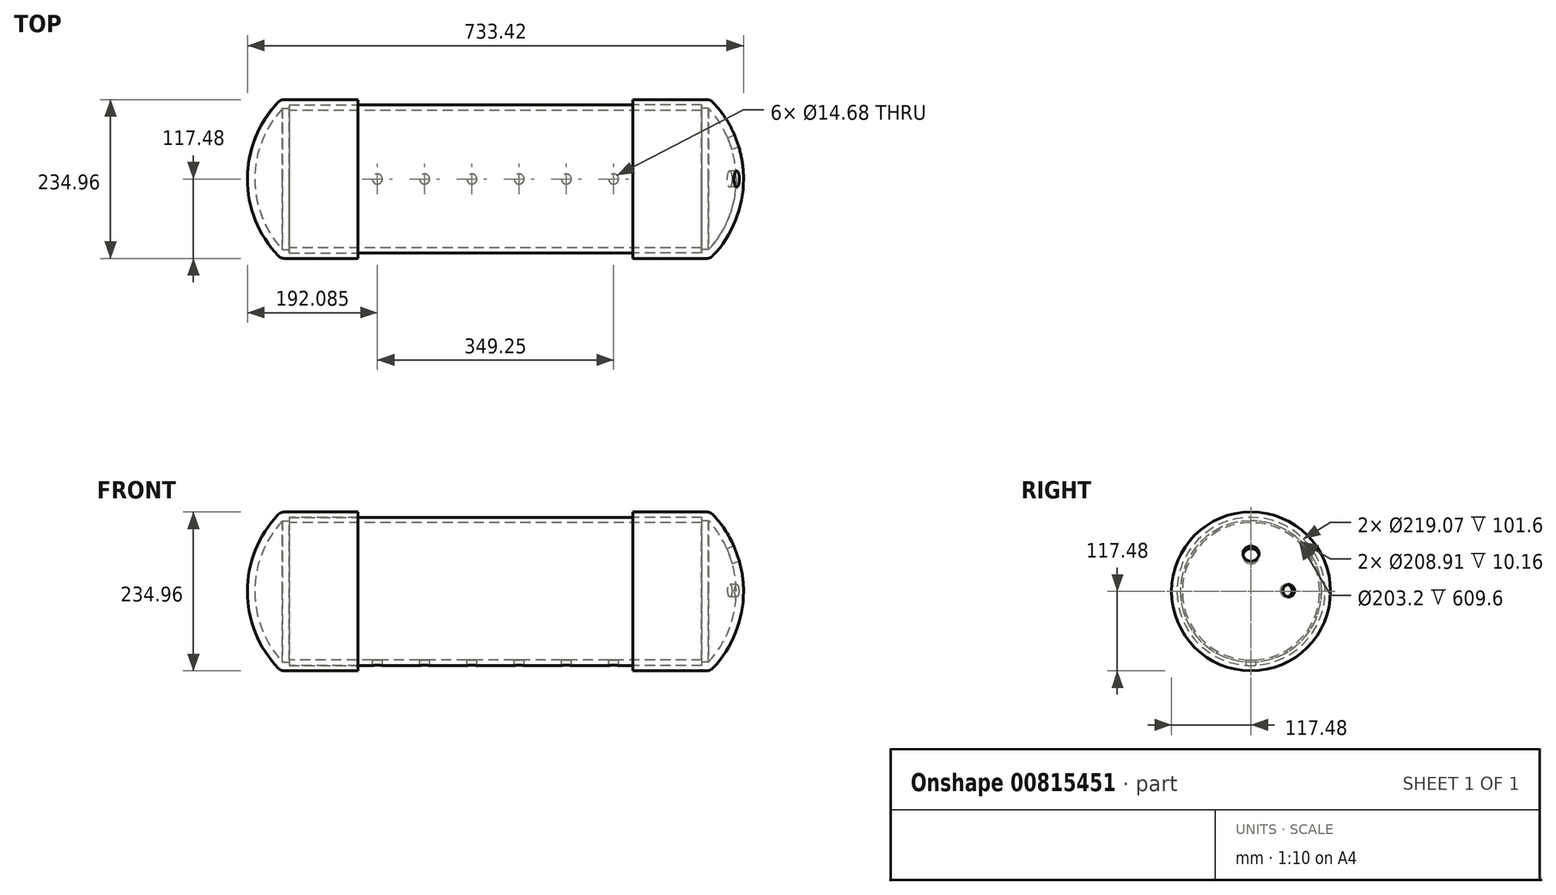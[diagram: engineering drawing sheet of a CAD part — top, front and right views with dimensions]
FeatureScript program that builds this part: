
annotation { "Feature Type Name" : "Feature", "Feature Type Description" : "" }
export const myFeature = defineFeature(function(context is Context, id is Id, definition is map)
    precondition{}
    {
        {
            var Q0;
            Q0=qCreatedBy(makeId("Right.planeOp"),FACE);
            var sketch = newSketch(context, id + "F0", { "sketchPlane" : qUnion([Q0])});
            skCircle(sketch, "E0", {"center": v(0, 0) * mm, "radius": 109.54 * mm});
            skCircle(sketch, "E1", {"center": v(0, 0) * mm, "radius": 101.6 * mm});
            skSolve(sketch);
        }
        {
            var Q0;
            Q0=makeQuery(id+"F0.imprint","IMPRINT",FACE,{"disambiguationData":[TD([[makeQuery(id+"F0.imprint","IMPRINT",EDGE,{"derivedFrom":sQuery(id+"F0.wireOp",EDGE,"E0")}),1.0]])]});
            extrude(context, id + "F1", {"entities" : qUnion([Q0]), "depth" : 304.8 * mm, "offsetDistance" : 25.4 * mm, "hasSecondDirection" : true, "secondDirectionOppositeDirection" : true, "secondDirectionDepth" : 304.8 * mm});
        }
        {
            var Q0;
            Q0=qCreatedBy(makeId("Top.planeOp"),FACE);
            var sketch = newSketch(context, id + "F2", { "sketchPlane" : qUnion([Q0])});
            skLineSegment(sketch, "E2", {"start": v(203.2, 109.54) * mm, "end": v(203.2, 117.48) * mm});
            skLineSegment(sketch, "E3", {"start": v(203.2, 117.48) * mm, "end": v(317.5, 117.48) * mm});
            skLineSegment(sketch, "E4", {"start": v(203.2, 109.54) * mm, "end": v(304.8, 109.54) * mm});
            skLineSegment(sketch, "E5", {"start": v(304.8, 109.54) * mm, "end": v(304.8, 104.46) * mm});
            skArc(sketch, "E6", {"start": v(317.5, 117.47) * mm, "mid": v(353.91, 63.68) * mm, "end": v(366.71, 0) * mm});
            skLineSegment(sketch, "E7", {"start": v(304.8, 104.46) * mm, "end": v(314.96, 104.46) * mm});
            skArc(sketch, "E8", {"start": v(314.96, 104.46) * mm, "mid": v(345.25, 56.08) * mm, "end": v(355.83, 0) * mm});
            skLineSegment(sketch, "E9", {"start": v(355.83, 0) * mm, "end": v(366.71, 0) * mm});
            skSolve(sketch);
        }
        {
            var Q0;
            Q0 = qSketchRegion(id + "F2", true);
            var Q1;
            Q1=sQuery(id+"F2.wireOp",EDGE,"E9");
            revolve(context, id + "F3", {"surfaceOperationType" : NewSurfaceOperationType.NEW, "entities" : qUnion([Q0]), "axis" : qUnion([Q1]), "revolveType" : RevolveType.FULL});
        }
        {
            var Q0;
            Q0=makeQuery(id+"F3.opRevolve","SWEPT_EDGE",EDGE,{"disambiguationData":[OSD([sQuery(id+"F2.wireOp",EDGE,"E3"),sQuery(id+"F2.wireOp",EDGE,"E6")])]});
            fillet(context, id + "F4", {"entities" : qUnion([Q0]), "radius" : 12.7 * mm, "tangentPropagation" : true, "allowEdgeOverflow" : false});
        }
        {
            var Q0;
            Q0=makeQuery(id+"F3.opRevolve","SWEPT_BODY",BODY,{"disambiguationData":[OSD([sQuery(id+"F2.wireOp",EDGE,"E2"),sQuery(id+"F2.wireOp",EDGE,"E3"),sQuery(id+"F2.wireOp",EDGE,"E4"),sQuery(id+"F2.wireOp",EDGE,"E5"),sQuery(id+"F2.wireOp",EDGE,"E6"),sQuery(id+"F2.wireOp",EDGE,"E7"),sQuery(id+"F2.wireOp",EDGE,"E8"),sQuery(id+"F2.wireOp",EDGE,"E9")])]});
            var Q1;
            Q1=qCreatedBy(makeId("Right.planeOp"),FACE);
            mirror(context, id + "F5", {"entities" : qUnion([Q0]), "mirrorPlane" : qUnion([Q1])});
        }
        {
            var Q0;
            Q0=makeQuery(id+"F3.opRevolve","SWEPT_FACE",FACE,{"disambiguationData":[OSD([sQuery(id+"F2.wireOp",EDGE,"E2")])]});
            var sketch = newSketch(context, id + "F6", { "sketchPlane" : qUnion([Q0])});
            skLineSegment(sketch, "E10", {"start": v(0, -22.41) * mm, "end": v(0, 24.56) * mm});
            skSolve(sketch);
        }
        {
            assignVariable(context, id + "F7", {"name" : "InSideAng", "anyValue" : 20});
        }
        {
            var Q0;
            Q0 = qBodyType(qCreatedBy(id + "F6" ,EDGE), BodyType.WIRE);
            cPlane(context, id + "F8", {"entities" : qUnion([Q0]), "cplaneType" : CPlaneType.LINE_ANGLE, "offset" : 25.4 * mm, "angle" : (getVariable(context, 'InSideAng')) * degree, "width" : 152.4 * mm, "height" : 152.4 * mm});
        }
        {
            var Q0;
            Q0=qCreatedBy(id+"F8.planeOp",FACE);
            var sketch = newSketch(context, id + "F9", { "sketchPlane" : qUnion([Q0])});
            skCircle(sketch, "E11", {"center": v(-69.5, 1.08) * mm, "radius": 9.13 * mm});
            skSolve(sketch);
        }
        {
            var Q0;
            Q0 = qSketchRegion(id + "F9", true);
            extrude(context, id + "F10", {"entities" : qUnion([Q0]), "operationType" : NewBodyOperationType.REMOVE, "endBound" : BoundingType.THROUGH_ALL, "depth" : 25.4 * mm, "offsetDistance" : 25.4 * mm});
        }
        {
            var Q0;
            Q0=qCreatedBy(makeId("Front.planeOp"),FACE);
            var sketch = newSketch(context, id + "F11", { "sketchPlane" : qUnion([Q0])});
            skLineSegment(sketch, "E12", {"start": v(-37.97, 0) * mm, "end": v(38.46, 0) * mm});
            skSolve(sketch);
        }
        {
            assignVariable(context, id + "F12", {"name" : "BotHoleAng", "anyValue" : 0});
        }
        {
            var Q0;
            Q0=sQuery(id+"F11.wireOp",EDGE,"E12");
            cPlane(context, id + "F13", {"entities" : qUnion([Q0]), "cplaneType" : CPlaneType.LINE_ANGLE, "offset" : 25.4 * mm, "angle" : (90 - (getVariable(context, 'BotHoleAng'))) * degree, "width" : 152.4 * mm, "height" : 152.4 * mm});
        }
        {
            var Q0;
            Q0=qCreatedBy(id+"F13.planeOp",FACE);
            var sketch = newSketch(context, id + "F14", { "sketchPlane" : qUnion([Q0])});
            skCircle(sketch, "E13", {"center": v(-174.63, 0) * mm, "radius": 7.34 * mm});
            skCircle(sketch, "E14.1.0.0", {"center": v(-104.78, 0) * mm, "radius": 7.34 * mm});
            skCircle(sketch, "E14.2.0.0", {"center": v(-34.93, 0) * mm, "radius": 7.34 * mm});
            skCircle(sketch, "E14.3.0.0", {"center": v(34.92, 0) * mm, "radius": 7.34 * mm});
            skCircle(sketch, "E14.4.0.0", {"center": v(104.77, 0) * mm, "radius": 7.34 * mm});
            skCircle(sketch, "E14.5.0.0", {"center": v(174.62, 0) * mm, "radius": 7.34 * mm});
            skLineSegment(sketch, "E14.direction1", {"start": v(-174.63, 0) * mm, "end": v(-104.78, 0) * mm, "construction": true});
            skSolve(sketch);
        }
        {
            var Q0;
            Q0 = qSketchRegion(id + "F14", true);
            extrude(context, id + "F15", {"entities" : qUnion([Q0]), "operationType" : NewBodyOperationType.REMOVE, "endBound" : BoundingType.THROUGH_ALL, "oppositeDirection" : true, "depth" : 156.97 * mm, "offsetDistance" : 25.4 * mm});
        }
        {
            assignVariable(context, id + "F16", {"name" : "OutSideAng", "anyValue" : 20});
        }
        {
            var Q0;
            Q0=sQuery(id+"F2.wireOp",EDGE,"E2");
            cPlane(context, id + "F17", {"entities" : qUnion([Q0]), "cplaneType" : CPlaneType.LINE_ANGLE, "offset" : 25.4 * mm, "angle" : ((90 - (getVariable(context, 'OutSideAng')))) * degree, "width" : 152.4 * mm, "height" : 152.4 * mm});
        }
        {
            var Q0;
            Q0=qCreatedBy(id+"F17.planeOp",FACE);
            var sketch = newSketch(context, id + "F18", { "sketchPlane" : qUnion([Q0])});
            skCircle(sketch, "E15", {"center": v(0, -69.5) * mm, "radius": 11.9 * mm});
            skSolve(sketch);
        }
        {
            var Q0;
            Q0 = qSketchRegion(id + "F18", true);
            extrude(context, id + "F19", {"entities" : qUnion([Q0]), "operationType" : NewBodyOperationType.REMOVE, "endBound" : BoundingType.THROUGH_ALL, "depth" : 25.4 * mm, "offsetDistance" : 25.4 * mm});
        }
    });
